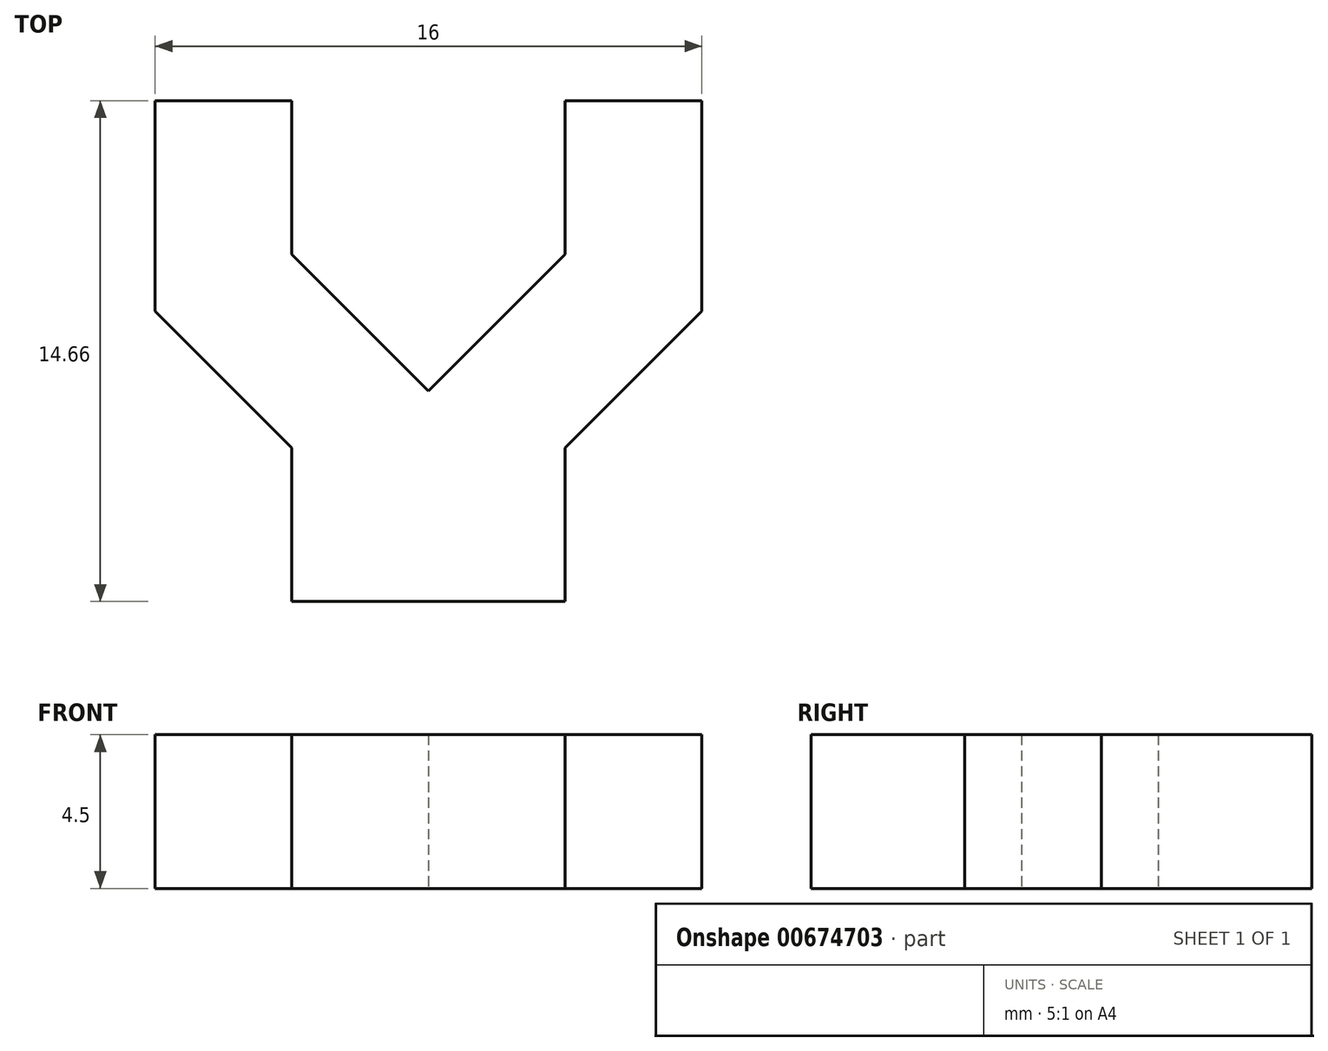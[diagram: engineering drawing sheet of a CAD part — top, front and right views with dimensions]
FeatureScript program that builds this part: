
annotation { "Feature Type Name" : "Feature", "Feature Type Description" : "" }
export const myFeature = defineFeature(function(context is Context, id is Id, definition is map)
    precondition{}
    {
        {
            var Q0;
            Q0=qCreatedBy(makeId("Top.planeOp"),FACE);
            var sketch = newSketch(context, id + "F0", { "sketchPlane" : qUnion([Q0])});
            skLineSegment(sketch, "E0", {"start": v(12.65, -1.09) * mm, "end": v(16.65, -1.09) * mm});
            skLineSegment(sketch, "E1", {"start": v(12.65, -1.09) * mm, "end": v(12.65, 5.07) * mm});
            skLineSegment(sketch, "E2", {"start": v(12.65, 5.07) * mm, "end": v(12.65, 20.92) * mm, "construction": true});
            skLineSegment(sketch, "E3", {"start": v(16.65, -1.09) * mm, "end": v(16.65, 19.23) * mm, "construction": true});
            skLineSegment(sketch, "E4", {"start": v(12.65, 5.07) * mm, "end": v(16.65, 9.07) * mm});
            skLineSegment(sketch, "E5", {"start": v(16.65, 9.07) * mm, "end": v(16.65, 13.57) * mm});
            skLineSegment(sketch, "E6", {"start": v(16.65, 13.57) * mm, "end": v(20.65, 13.57) * mm});
            skLineSegment(sketch, "E7", {"start": v(20.65, 13.57) * mm, "end": v(20.65, 7.41) * mm});
            skLineSegment(sketch, "E8", {"start": v(20.65, 7.41) * mm, "end": v(16.65, 3.41) * mm});
            skLineSegment(sketch, "E9", {"start": v(16.65, 3.41) * mm, "end": v(16.65, -1.09) * mm});
            skLineSegment(sketch, "E10", {"start": v(13.6, 11.57) * mm, "end": v(25.3, 11.57) * mm, "construction": true});
            skLineSegment(sketch, "E11", {"start": v(20.36, 0.91) * mm, "end": v(10.32, 0.91) * mm, "construction": true});
            skLineSegment(sketch, "E12.MirrorCS", {"start": v(11.7, 11.57) * mm, "end": v(0, 11.57) * mm, "construction": true});
            skLineSegment(sketch, "E13.MirrorCS", {"start": v(8.65, 9.07) * mm, "end": v(8.65, 13.57) * mm});
            skLineSegment(sketch, "E14.MirrorCS", {"start": v(12.65, -1.09) * mm, "end": v(8.65, -1.09) * mm});
            skLineSegment(sketch, "E15.MirrorCS", {"start": v(12.65, 5.07) * mm, "end": v(8.65, 9.07) * mm});
            skLineSegment(sketch, "E16.MirrorCS", {"start": v(8.65, 3.41) * mm, "end": v(8.65, -1.09) * mm});
            skLineSegment(sketch, "E17.MirrorCS", {"start": v(8.65, -1.09) * mm, "end": v(8.65, 19.23) * mm, "construction": true});
            skLineSegment(sketch, "E18.MirrorCS", {"start": v(4.65, 7.41) * mm, "end": v(8.65, 3.41) * mm});
            skLineSegment(sketch, "E19.MirrorCS", {"start": v(4.65, 13.57) * mm, "end": v(4.65, 7.41) * mm});
            skLineSegment(sketch, "E20.MirrorCS", {"start": v(8.65, 13.57) * mm, "end": v(4.65, 13.57) * mm});
            skLineSegment(sketch, "E21.MirrorCS", {"start": v(4.94, 0.91) * mm, "end": v(14.98, 0.91) * mm, "construction": true});
            skSolve(sketch);
        }
        {
            var Q0;
            Q0=makeQuery(id+"F0.imprint","IMPRINT",FACE,{"disambiguationData":[TD([[makeQuery(id+"F0.imprint","IMPRINT",EDGE,{"derivedFrom":sQuery(id+"F0.wireOp",EDGE,"E0")}),1.0]])]});
            var Q1;
            Q1=makeQuery(id+"F0.imprint","IMPRINT",FACE,{"disambiguationData":[TD([[makeQuery(id+"F0.imprint","IMPRINT",EDGE,{"derivedFrom":sQuery(id+"F0.wireOp",EDGE,"E13.MirrorCS")}),1.0]])]});
            extrude(context, id + "F1", {"entities" : qUnion([Q0, Q1]), "depth" : 4.5 * mm, "offsetDistance" : 25 * mm});
        }
    });
